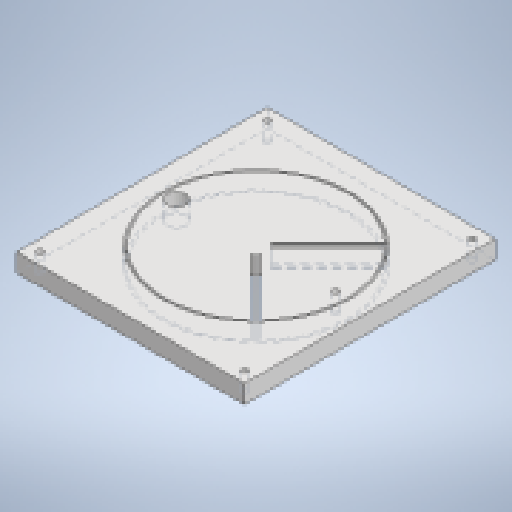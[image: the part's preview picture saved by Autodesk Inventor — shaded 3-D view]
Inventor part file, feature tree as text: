
AUTODESK INVENTOR PART (.ipt)
format: ipt  version: 2023 (Build 270158000, 158)  size: 215,040 bytes
history: native  units: mm
features: extrude x3, sketch x2
ambient origin geometry x8: Origin, YZ Plane, XZ Plane, XY Plane, X Axis, Y Axis, Z Axis, Center Point
bodies: Solid1 (feature_tree)
feature tree (5):
  extrude  "Extrusion1"  Depth=110.0mm
  extrude  "Extrusion2"  TaperAngle=0.0deg  [1 undecoded]
  extrude  "Extrusion5"  Depth=1.0mm
  sketch  "Sketch1"  dims[d0=100.0mm d1=110.0mm]
  sketch  "Sketch8"  dims[d2=0.0mm d3=0.0mm d4=150.0mm d5=150.0mm d6=8.0mm d7=0.0mm d18=45.0mm d19=45.0mm d21=47.0mm d22=47.0mm d85=20.0mm d86=0.0mm d118=5.0mm d119=5.0mm d120=2.65mm d132=50.0mm d133=55.0mm d134=10.0mm d135=80.0mm d136=82.0mm d145=35.0mm d146=0.0mm d147=2.75mm d153=20.0mm d154=0.0mm d155=8.0mm d156=35.0mm d157=45.0deg d158=0.5mm d159=0.5mm d160=1.0mm d161=1.0mm d162=20.0mm d164=90.0deg]
note: 1 required parameter value undecoded (feature->parameter linkage not recoverable at this tier; creation-order binding heuristic only, values carry confidence <= 0.55)
